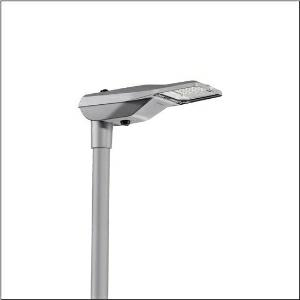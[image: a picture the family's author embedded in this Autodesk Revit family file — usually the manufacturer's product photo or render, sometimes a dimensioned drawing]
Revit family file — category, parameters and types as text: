
# Revit family: streetlight_sl_21_iq_micro___st1_0a_5xe1d51y08db_19c1
name_source: partatom
category: Lighting Fixtures
units: mm (PartAtom-declared; Revit-internal decimal feet)

## family parameters
Cut with Voids When Loaded = No
Host = Face
Light Source = No
Part Type = Normal
Room Calculation Point = No
Round Connector Dimension = Use Diameter
Shared = No

## types (1)
- --- (1 x LED, 4490 lm, 39.1 W, 3000K)
    Apparent Load = 39 VA
    CIE Flux Codes = 37 72 97 100 100
    Color Rendering = 80
    Color Temperature = 3000K
    Default Elevation = 1800 mm
    Description = Streetlight SL 21 iQ micro, mast luminaire, primary light control with lens, of PMMA, primary optical cover: cover, of toughened safety glass, transparent, light distribution: ST1.0a, light emission: direct distribution, primary light characteristic: asymmetric, installation type: post-top, side-entry, LED, High Power LED, rated luminous flux: 4.490lm, luminous efficacy: 115lm/W, light colour: 830, colour temperature: 3000K, control gear: iQ-Street Remote, D4i with power reduction, control: pre-setting: logarithmic dimming characteristic, Street-Remote, Auto-Match, Temp-Guard, Lumen-Switch, Night-Set, Smart-Wire, Light-Fading, Desk-Remote (wireless, voltage-free reading and setting of iQ features in the workshop via application-optimized NFC function/RFID function), optimised constant luminous flux control (CLO 2.0), mains connection: 220..240V, AC, 50/60Hz, start of lifetime: 39W, end of service life: 41W, reduction: 17W, luminaire housing, of diecast aluminium, powder-coated, Siteco® metallic grey (DB 702S), corrosivity category C5 mid according to DIN EN ISO 12944, please order mast flange separately, inclination adjustable: 0°, 5°, 10°, 15°, sealing non-destructively replaceable, multi-level sealing system, length: 528mm, width: 235mm, height: 110mm, mast flange for spigot size: 42mm (side-entry): 5XC10008XM4, 60/48mm (side-entry/post-top): 5XC10108XM2, 76/60mm (side-entry/post-top): 5XC10108XM1, mounting height: 4..8m, Smart Interface below and above, protection rating (complete): IP66, insulation class (complete): insulation class II (safety insulation), certification: CE, ENEC, ENEC+, VDE, impact resistance: IK10, permissible operating ambient temperature for outdoor applications: -40..+50°C, standard-compliant lighting for roads and squares, packaging unit: 1 piece

Light Distribution: ST1.0a
    Height = 110 mm
    Lamp = 1 x LED
    Lamp Light Flux = 4490 lm
    Lamp Power = 39.1 W
    Lamp count = 1
    Length = 528 mm
    Luminous efficacy = 115 lm/W
    Manufacturer = Siteco
    ModVariant = No
    Model = 5XE1D51Y08DB
    Number of Poles = 1
    OnlyDefault = Yes
    Power Factor = 1
    Product Name = Streetlight SL 21 iQ micro | ST1.0a
    Product group = mast luminaire | pylon top
    ProductGroupID = 6100
    Protection Class = Protection class II
    Protection Degree = IP 66
    RLX_Detail_Level = 1
    RLX_Emergency_Light_Flux = 0 lm
    RLX_Emergency_Type = 0
    RLX_Emergency_Type_DB = No
    RlxData = <blob elided: 98577 chars, md5=a60c0649>
    Socket = socket
    Standby Power = 0 W
    System Light Flux = 4490 lm
    System Power = 39 W
    Type Comments = factory setting: luminous flux: 100 % | dim-lin: 254 | 765 mA
    Type Image = l_1007239.jpg
    URL = http://relux.com
    VarID = @adj_136819
    Voltage = 0 V
    Weight = 0.00 kg
    Width = 235 mm

## geometry (parser evidence)
native form markers: Blend x4, Sweep x10
no freeform markers — native parametric forms only
